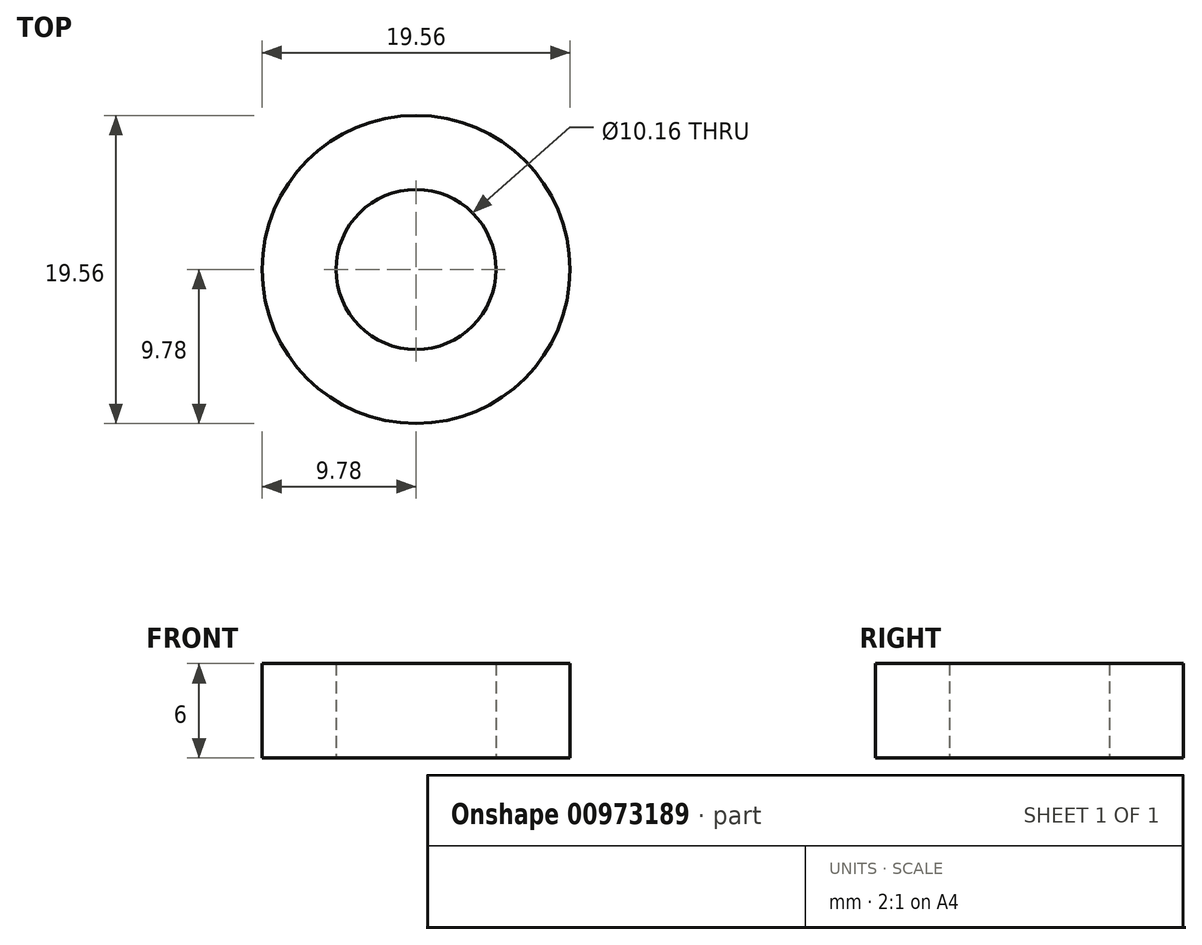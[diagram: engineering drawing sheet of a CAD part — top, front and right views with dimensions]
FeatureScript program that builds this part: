
annotation { "Feature Type Name" : "Feature", "Feature Type Description" : "" }
export const myFeature = defineFeature(function(context is Context, id is Id, definition is map)
    precondition{}
    {
        {
            var Q0;
            Q0=qCreatedBy(makeId("Top.planeOp"),FACE);
            var sketch = newSketch(context, id + "F0", { "sketchPlane" : qUnion([Q0])});
            skCircle(sketch, "E0", {"center": v(0, 0) * mm, "radius": 5.08 * mm});
            skCircle(sketch, "E1", {"center": v(0, 0) * mm, "radius": 9.78 * mm});
            skSolve(sketch);
        }
        {
            var Q0;
            Q0=qSketchRegion(id+"F0",true);
            extrude(context, id + "F1", {"entities" : qUnion([Q0]), "depth" : 6 * mm, "offsetDistance" : 25.4 * mm});
        }
    });
